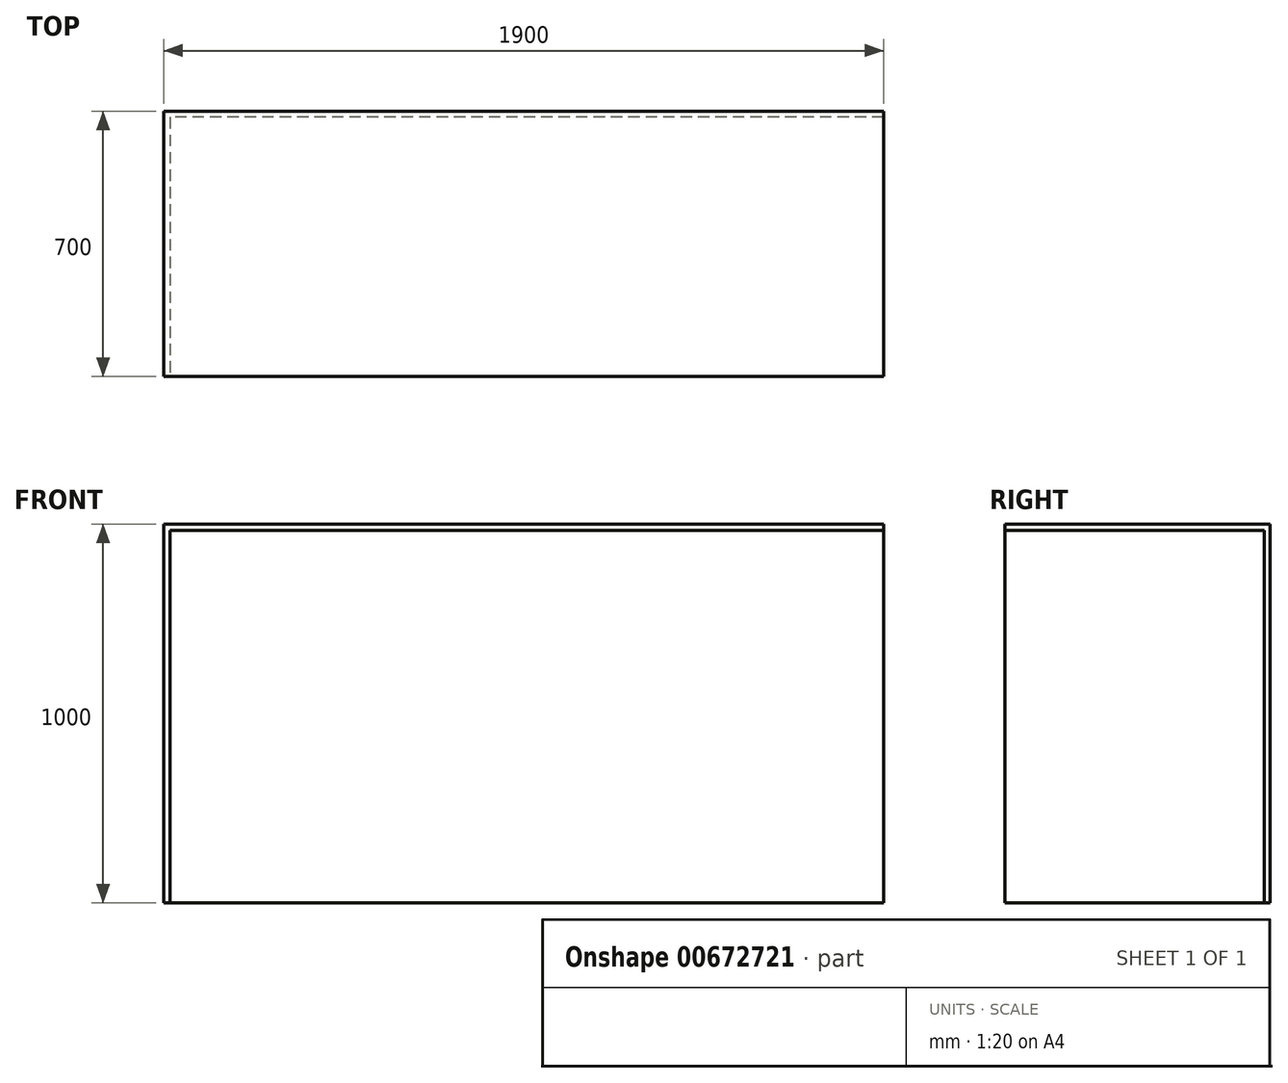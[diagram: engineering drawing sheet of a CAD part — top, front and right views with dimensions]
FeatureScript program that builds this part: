
annotation { "Feature Type Name" : "Feature", "Feature Type Description" : "" }
export const myFeature = defineFeature(function(context is Context, id is Id, definition is map)
    precondition{}
    {
        {
            var Q0;
            Q0=qCreatedBy(makeId("Top.planeOp"),FACE);
            var sketch = newSketch(context, id + "F0", { "sketchPlane" : qUnion([Q0])});
            skLineSegment(sketch, "E0.bottom", {"start": v(0, 0) * mm, "end": v(-1900, 0) * mm});
            skLineSegment(sketch, "E0.top", {"start": v(0, -700) * mm, "end": v(-1900, -700) * mm});
            skLineSegment(sketch, "E0.left", {"start": v(0, 0) * mm, "end": v(0, -700) * mm});
            skLineSegment(sketch, "E0.right", {"start": v(-1900, 0) * mm, "end": v(-1900, -700) * mm});
            skSolve(sketch);
        }
        {
            var Q0;
            Q0=makeQuery(id+"F0.imprint","IMPRINT",FACE,{"disambiguationData":[TD([[makeQuery(id+"F0.imprint","IMPRINT",EDGE,{"derivedFrom":sQuery(id+"F0.wireOp",EDGE,"Y66rWitT-qBWe-ztKi-yuPp-pPcdfemAuZkT.bottom")}),-1.0]])]});
            var Q1;
            Q1=makeQuery(id+"F0.imprint","IMPRINT",FACE,{"disambiguationData":[TD([[makeQuery(id+"F0.imprint","IMPRINT",EDGE,{"derivedFrom":sQuery(id+"F0.wireOp",EDGE,"E0.bottom")}),1.0]])]});
            extrude(context, id + "F1", {"entities" : qUnion([Q0, Q1]), "depth" : 1000 * mm, "offsetDistance" : 25 * mm});
        }
        {
            var Q0;
            Q0=makeQuery(id+"F1.opExtrude","CAP_FACE",FACE,{"disambiguationData":[OSD([sQuery(id+"F0.wireOp",EDGE,"E0.bottom"),sQuery(id+"F0.wireOp",EDGE,"E0.top"),sQuery(id+"F0.wireOp",EDGE,"E0.left"),sQuery(id+"F0.wireOp",EDGE,"E0.right")])],"isStart":true});
            var Q1;
            Q1=makeQuery(id+"F1.opExtrude","SWEPT_FACE",FACE,{"disambiguationData":[OSD([sQuery(id+"F0.wireOp",EDGE,"E0.top")])]});
            var Q2;
            Q2=makeQuery(id+"F1.opExtrude","SWEPT_FACE",FACE,{"disambiguationData":[OSD([sQuery(id+"F0.wireOp",EDGE,"E0.left")])]});
            shell(context, id + "F2", {"entities" : qUnion([Q0, Q1, Q2]), "thickness" : 16 * mm});
        }
    });
